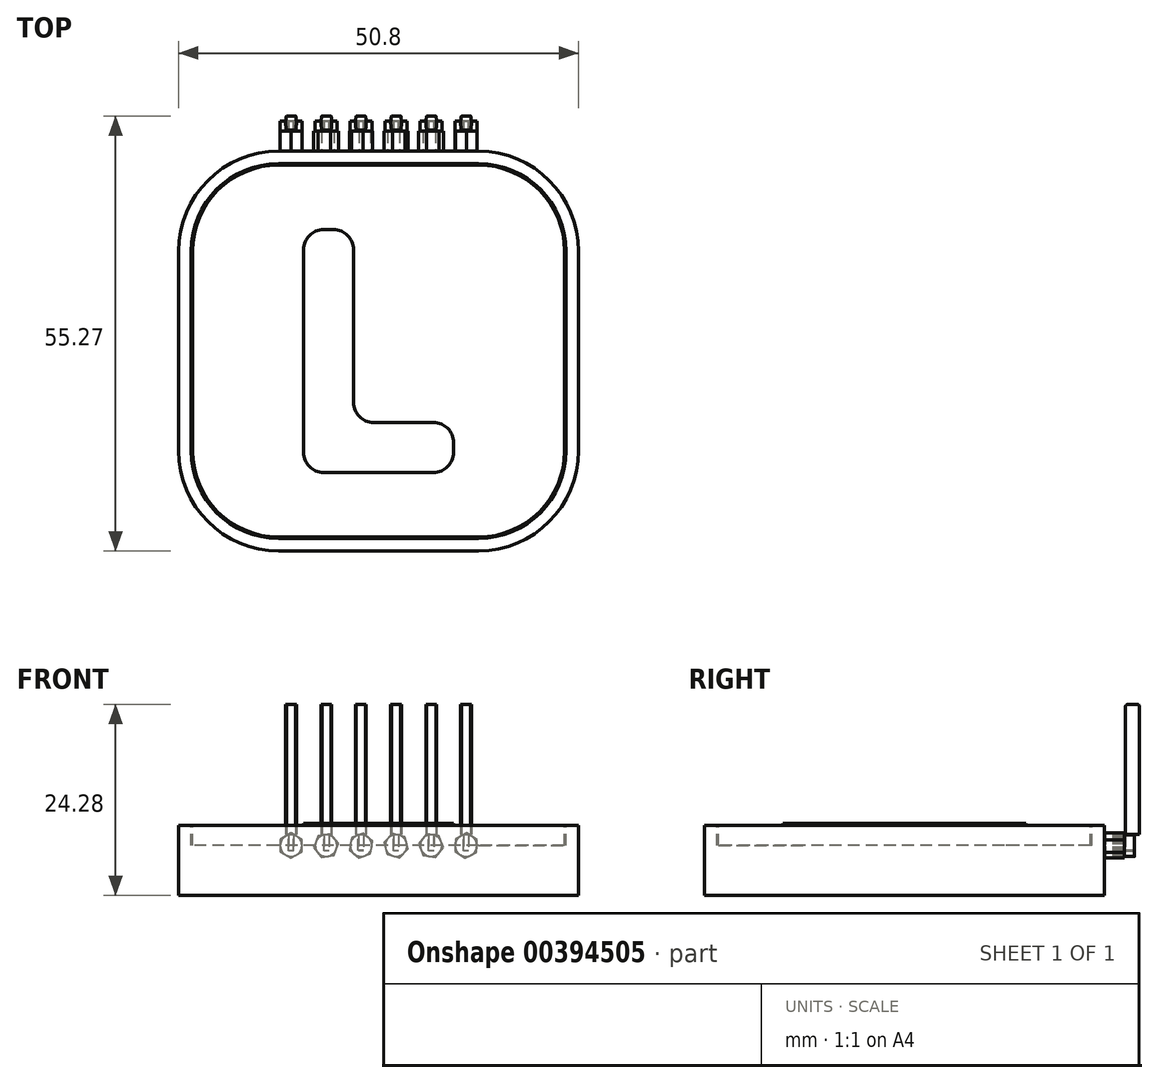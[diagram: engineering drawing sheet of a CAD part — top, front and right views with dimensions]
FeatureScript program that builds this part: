
annotation { "Feature Type Name" : "Feature", "Feature Type Description" : "" }
export const myFeature = defineFeature(function(context is Context, id is Id, definition is map)
    precondition{}
    {
        {
            var Q0;
            Q0=qCreatedBy(makeId("Top.planeOp"),FACE);
            var sketch = newSketch(context, id + "F0", { "sketchPlane" : qUnion([Q0])});
            skLineSegment(sketch, "E0.bottom", {"start": v(-25.4, 25.4) * mm, "end": v(25.4, 25.4) * mm});
            skLineSegment(sketch, "E0.top", {"start": v(-25.4, -25.4) * mm, "end": v(25.4, -25.4) * mm});
            skLineSegment(sketch, "E0.left", {"start": v(-25.4, 25.4) * mm, "end": v(-25.4, -25.4) * mm});
            skLineSegment(sketch, "E0.right", {"start": v(25.4, 25.4) * mm, "end": v(25.4, -25.4) * mm});
            skSolve(sketch);
        }
        {
            var Q0;
            Q0=makeQuery(id+"F0.imprint","IMPRINT",FACE,{"disambiguationData":[TD([[makeQuery(id+"F0.imprint","IMPRINT",EDGE,{"derivedFrom":sQuery(id+"F0.wireOp",EDGE,"E0.bottom")}),-1.0]])]});
            extrude(context, id + "F1", {"entities" : qUnion([Q0]), "depth" : 8.9 * mm});
        }
        {
            var Q0;
            Q0=makeQuery(id+"F1.opExtrude","SWEPT_EDGE",EDGE,{"disambiguationData":[OSD([sQuery(id+"F0.wireOp",EDGE,"E0.top"),sQuery(id+"F0.wireOp",EDGE,"E0.left")])]});
            var Q1;
            Q1=makeQuery(id+"F1.opExtrude","SWEPT_EDGE",EDGE,{"disambiguationData":[OSD([sQuery(id+"F0.wireOp",EDGE,"E0.bottom"),sQuery(id+"F0.wireOp",EDGE,"E0.left")])]});
            var Q2;
            Q2=makeQuery(id+"F1.opExtrude","SWEPT_EDGE",EDGE,{"disambiguationData":[OSD([sQuery(id+"F0.wireOp",EDGE,"E0.top"),sQuery(id+"F0.wireOp",EDGE,"E0.right")])]});
            var Q3;
            Q3=makeQuery(id+"F1.opExtrude","SWEPT_EDGE",EDGE,{"disambiguationData":[OSD([sQuery(id+"F0.wireOp",EDGE,"E0.bottom"),sQuery(id+"F0.wireOp",EDGE,"E0.right")])]});
            fillet(context, id + "F2", {"entities" : qUnion([Q0, Q1, Q2, Q3]), "radius" : 12.7 * mm, "tangentPropagation" : true, "allowEdgeOverflow" : false});
        }
        {
            var Q0;
            Q0=makeQuery(id+"F1.opExtrude","CAP_FACE",FACE,{"disambiguationData":[OSD([sQuery(id+"F0.wireOp",EDGE,"E0.bottom"),sQuery(id+"F0.wireOp",EDGE,"E0.top"),sQuery(id+"F0.wireOp",EDGE,"E0.left"),sQuery(id+"F0.wireOp",EDGE,"E0.right")])],"isStart":false});
            var sketch = newSketch(context, id + "F3", { "sketchPlane" : qUnion([Q0])});
            skArc(sketch, "E1.0", {"start": v(-12.7, 23.81) * mm, "mid": v(-20.56, 20.56) * mm, "end": v(-23.81, 12.7) * mm});
            skLineSegment(sketch, "E1.1", {"start": v(12.7, 23.81) * mm, "end": v(-12.7, 23.81) * mm});
            skLineSegment(sketch, "E1.2", {"start": v(-23.81, 12.7) * mm, "end": v(-23.81, -12.7) * mm});
            skArc(sketch, "E1.3", {"start": v(23.81, 12.7) * mm, "mid": v(20.56, 20.56) * mm, "end": v(12.7, 23.81) * mm});
            skArc(sketch, "E1.4", {"start": v(-23.81, -12.7) * mm, "mid": v(-20.56, -20.56) * mm, "end": v(-12.7, -23.81) * mm});
            skLineSegment(sketch, "E1.5", {"start": v(-12.7, -23.81) * mm, "end": v(12.7, -23.81) * mm});
            skArc(sketch, "E1.6", {"start": v(12.7, -23.81) * mm, "mid": v(20.56, -20.56) * mm, "end": v(23.81, -12.7) * mm});
            skLineSegment(sketch, "E1.7", {"start": v(23.81, -12.7) * mm, "end": v(23.81, 12.7) * mm});
            skArc(sketch, "E2.0", {"start": v(-12.7, 23.62) * mm, "mid": v(-20.42, 20.42) * mm, "end": v(-23.62, 12.7) * mm});
            skLineSegment(sketch, "E2.1", {"start": v(12.7, 23.62) * mm, "end": v(-12.7, 23.62) * mm});
            skLineSegment(sketch, "E2.2", {"start": v(-23.62, 12.7) * mm, "end": v(-23.62, -12.7) * mm});
            skArc(sketch, "E2.3", {"start": v(23.62, 12.7) * mm, "mid": v(20.42, 20.42) * mm, "end": v(12.7, 23.62) * mm});
            skArc(sketch, "E2.4", {"start": v(-23.62, -12.7) * mm, "mid": v(-20.42, -20.42) * mm, "end": v(-12.7, -23.62) * mm});
            skLineSegment(sketch, "E2.5", {"start": v(-12.7, -23.62) * mm, "end": v(12.7, -23.62) * mm});
            skArc(sketch, "E2.6", {"start": v(12.7, -23.62) * mm, "mid": v(20.42, -20.42) * mm, "end": v(23.62, -12.7) * mm});
            skLineSegment(sketch, "E2.7", {"start": v(23.62, -12.7) * mm, "end": v(23.62, 12.7) * mm});
            skSolve(sketch);
        }
        {
            var Q0;
            Q0=makeQuery(id+"F3.imprint","IMPRINT",FACE,{"disambiguationData":[TD([[makeQuery(id+"F3.imprint","IMPRINT",EDGE,{"derivedFrom":sQuery(id+"F3.wireOp",EDGE,"E1.0")}),1.0]])]});
            extrude(context, id + "F4", {"entities" : qUnion([Q0]), "operationType" : NewBodyOperationType.REMOVE, "oppositeDirection" : true, "depth" : 2.54 * mm});
        }
        {
            var Q0;
            Q0=makeQuery(id+"F4.boolean.opBoolean","SPLIT",FACE,{"disambiguationData":[TD([makeQuery(id+"F4.opExtrude","SWEPT_FACE",FACE,{"disambiguationData":[OSD([sQuery(id+"F3.wireOp",EDGE,"E2.0")])]})])],"derivedFrom":makeQuery(id+"F1.opExtrude","CAP_FACE",FACE,{"disambiguationData":[OSD([sQuery(id+"F0.wireOp",EDGE,"E0.bottom"),sQuery(id+"F0.wireOp",EDGE,"E0.top"),sQuery(id+"F0.wireOp",EDGE,"E0.left"),sQuery(id+"F0.wireOp",EDGE,"E0.right")])],"isStart":false})});
            var sketch = newSketch(context, id + "F5", { "sketchPlane" : qUnion([Q0])});
            skLineSegment(sketch, "E3", {"start": v(-9.53, 15.42) * mm, "end": v(-9.52, -15.42) * mm});
            skLineSegment(sketch, "E4", {"start": v(-9.52, -15.42) * mm, "end": v(9.53, -15.42) * mm});
            skLineSegment(sketch, "E5", {"start": v(9.53, -9.07) * mm, "end": v(-3.18, -9.07) * mm});
            skLineSegment(sketch, "E6", {"start": v(-3.18, -9.07) * mm, "end": v(-3.18, 15.42) * mm});
            skLineSegment(sketch, "E7", {"start": v(-3.18, 15.42) * mm, "end": v(-9.53, 15.42) * mm});
            skLineSegment(sketch, "E8", {"start": v(9.53, -9.07) * mm, "end": v(9.53, -15.42) * mm});
            skLineSegment(sketch, "E9.0", {"start": v(9.78, -8.81) * mm, "end": v(-2.92, -8.81) * mm});
            skLineSegment(sketch, "E9.1", {"start": v(-2.92, 15.67) * mm, "end": v(-9.78, 15.67) * mm});
            skLineSegment(sketch, "E9.2", {"start": v(-9.78, 15.67) * mm, "end": v(-9.78, -15.67) * mm});
            skLineSegment(sketch, "E9.3", {"start": v(-2.92, -8.81) * mm, "end": v(-2.92, 15.67) * mm});
            skLineSegment(sketch, "E9.4", {"start": v(-9.78, -15.67) * mm, "end": v(9.78, -15.67) * mm});
            skLineSegment(sketch, "E9.5", {"start": v(9.78, -8.81) * mm, "end": v(9.78, -15.67) * mm});
            skSolve(sketch);
        }
        {
            var Q0;
            Q0=makeQuery(id+"F5.imprint","IMPRINT",FACE,{"disambiguationData":[TD([[makeQuery(id+"F5.imprint","IMPRINT",EDGE,{"derivedFrom":sQuery(id+"F5.wireOp",EDGE,"E3")}),1.0]])]});
            extrude(context, id + "F6", {"entities" : qUnion([Q0]), "depth" : 0.25 * mm});
        }
        {
            var Q0;
            Q0=makeQuery(id+"F6.opExtrude","SWEPT_EDGE",EDGE,{"disambiguationData":[OSD([sQuery(id+"F5.wireOp",EDGE,"E3"),sQuery(id+"F5.wireOp",EDGE,"E4")])]});
            var Q1;
            Q1=makeQuery(id+"F6.opExtrude","SWEPT_EDGE",EDGE,{"disambiguationData":[OSD([sQuery(id+"F5.wireOp",EDGE,"E4"),sQuery(id+"F5.wireOp",EDGE,"E8")])]});
            var Q2;
            Q2=makeQuery(id+"F6.opExtrude","SWEPT_EDGE",EDGE,{"disambiguationData":[OSD([sQuery(id+"F5.wireOp",EDGE,"E5"),sQuery(id+"F5.wireOp",EDGE,"E8")])]});
            var Q3;
            Q3=makeQuery(id+"F6.opExtrude","SWEPT_EDGE",EDGE,{"disambiguationData":[OSD([sQuery(id+"F5.wireOp",EDGE,"E5"),sQuery(id+"F5.wireOp",EDGE,"E6")])]});
            var Q4;
            Q4=makeQuery(id+"F6.opExtrude","SWEPT_EDGE",EDGE,{"disambiguationData":[OSD([sQuery(id+"F5.wireOp",EDGE,"E6"),sQuery(id+"F5.wireOp",EDGE,"E7")])]});
            var Q5;
            Q5=makeQuery(id+"F6.opExtrude","SWEPT_EDGE",EDGE,{"disambiguationData":[OSD([sQuery(id+"F5.wireOp",EDGE,"E3"),sQuery(id+"F5.wireOp",EDGE,"E7")])]});
            fillet(context, id + "F7", {"entities" : qUnion([Q0, Q1, Q2, Q3, Q4, Q5]), "radius" : 2.54 * mm, "tangentPropagation" : true, "allowEdgeOverflow" : false});
        }
        {
            var Q0;
            Q0=makeQuery(id+"F1.opExtrude","SWEPT_FACE",FACE,{"disambiguationData":[OSD([sQuery(id+"F0.wireOp",EDGE,"E0.bottom")])]});
            var sketch = newSketch(context, id + "F8", { "sketchPlane" : qUnion([Q0])});
            skLineSegment(sketch, "E10.0", {"start": v(-9.71, 5.6) * mm, "end": v(-11.06, 4.76) * mm});
            skLineSegment(sketch, "E10.1", {"start": v(-11.06, 4.76) * mm, "end": v(-12.46, 5.5) * mm});
            skLineSegment(sketch, "E10.2", {"start": v(-12.46, 5.5) * mm, "end": v(-12.51, 7.1) * mm});
            skLineSegment(sketch, "E10.3", {"start": v(-12.51, 7.1) * mm, "end": v(-11.17, 7.94) * mm});
            skLineSegment(sketch, "E10.4", {"start": v(-11.17, 7.94) * mm, "end": v(-9.77, 7.2) * mm});
            skLineSegment(sketch, "E10.5", {"start": v(-9.77, 7.2) * mm, "end": v(-9.71, 5.6) * mm});
            skLineSegment(sketch, "E11.0", {"start": v(-7.25, 4.87) * mm, "end": v(-8.24, 6.12) * mm});
            skLineSegment(sketch, "E11.1", {"start": v(-8.24, 6.12) * mm, "end": v(-7.65, 7.6) * mm});
            skLineSegment(sketch, "E11.2", {"start": v(-7.65, 7.6) * mm, "end": v(-6.08, 7.83) * mm});
            skLineSegment(sketch, "E11.3", {"start": v(-6.08, 7.83) * mm, "end": v(-5.1, 6.58) * mm});
            skLineSegment(sketch, "E11.4", {"start": v(-5.1, 6.58) * mm, "end": v(-5.68, 5.1) * mm});
            skLineSegment(sketch, "E11.5", {"start": v(-5.68, 5.1) * mm, "end": v(-7.25, 4.87) * mm});
            skLineSegment(sketch, "E12.0", {"start": v(-2.64, 4.82) * mm, "end": v(-3.76, 5.95) * mm});
            skLineSegment(sketch, "E12.1", {"start": v(-3.76, 5.95) * mm, "end": v(-3.34, 7.48) * mm});
            skLineSegment(sketch, "E12.2", {"start": v(-3.34, 7.48) * mm, "end": v(-1.8, 7.88) * mm});
            skLineSegment(sketch, "E12.3", {"start": v(-1.8, 7.88) * mm, "end": v(-0.69, 6.75) * mm});
            skLineSegment(sketch, "E12.4", {"start": v(-0.69, 6.75) * mm, "end": v(-1.1, 5.22) * mm});
            skLineSegment(sketch, "E12.5", {"start": v(-1.1, 5.22) * mm, "end": v(-2.64, 4.82) * mm});
            skLineSegment(sketch, "E13.0", {"start": v(2.47, 4.78) * mm, "end": v(0.99, 5.35) * mm});
            skLineSegment(sketch, "E13.1", {"start": v(0.99, 5.35) * mm, "end": v(0.74, 6.92) * mm});
            skLineSegment(sketch, "E13.2", {"start": v(0.74, 6.92) * mm, "end": v(1.97, 7.92) * mm});
            skLineSegment(sketch, "E13.3", {"start": v(1.97, 7.92) * mm, "end": v(3.46, 7.35) * mm});
            skLineSegment(sketch, "E13.4", {"start": v(3.46, 7.35) * mm, "end": v(3.7, 5.78) * mm});
            skLineSegment(sketch, "E13.5", {"start": v(3.7, 5.78) * mm, "end": v(2.47, 4.78) * mm});
            skLineSegment(sketch, "E14.0", {"start": v(5.67, 5.12) * mm, "end": v(5.1, 6.6) * mm});
            skLineSegment(sketch, "E14.1", {"start": v(5.1, 6.6) * mm, "end": v(6.1, 7.83) * mm});
            skLineSegment(sketch, "E14.2", {"start": v(6.1, 7.83) * mm, "end": v(7.67, 7.58) * mm});
            skLineSegment(sketch, "E14.3", {"start": v(7.67, 7.58) * mm, "end": v(8.23, 6.1) * mm});
            skLineSegment(sketch, "E14.4", {"start": v(8.23, 6.1) * mm, "end": v(7.23, 4.87) * mm});
            skLineSegment(sketch, "E14.5", {"start": v(7.23, 4.87) * mm, "end": v(5.67, 5.12) * mm});
            skLineSegment(sketch, "E15.0", {"start": v(11.11, 4.76) * mm, "end": v(9.74, 5.56) * mm});
            skLineSegment(sketch, "E15.1", {"start": v(9.74, 5.56) * mm, "end": v(9.74, 7.14) * mm});
            skLineSegment(sketch, "E15.2", {"start": v(9.74, 7.14) * mm, "end": v(11.11, 7.94) * mm});
            skLineSegment(sketch, "E15.3", {"start": v(11.11, 7.94) * mm, "end": v(12.49, 7.14) * mm});
            skLineSegment(sketch, "E15.4", {"start": v(12.49, 7.14) * mm, "end": v(12.49, 5.56) * mm});
            skLineSegment(sketch, "E15.5", {"start": v(12.49, 5.56) * mm, "end": v(11.11, 4.76) * mm});
            skSolve(sketch);
        }
        {
            var Q0;
            Q0=makeQuery(id+"F8.imprint","IMPRINT",FACE,{"disambiguationData":[TD([[makeQuery(id+"F8.imprint","IMPRINT",EDGE,{"derivedFrom":sQuery(id+"F8.wireOp",EDGE,"E10.0")}),-1.0]])]});
            var Q1;
            Q1=makeQuery(id+"F8.imprint","IMPRINT",FACE,{"disambiguationData":[TD([[makeQuery(id+"F8.imprint","IMPRINT",EDGE,{"derivedFrom":sQuery(id+"F8.wireOp",EDGE,"E11.0")}),-1.0]])]});
            var Q2;
            Q2=makeQuery(id+"F8.imprint","IMPRINT",FACE,{"disambiguationData":[TD([[makeQuery(id+"F8.imprint","IMPRINT",EDGE,{"derivedFrom":sQuery(id+"F8.wireOp",EDGE,"E12.0")}),-1.0]])]});
            var Q3;
            Q3=makeQuery(id+"F8.imprint","IMPRINT",FACE,{"disambiguationData":[TD([[makeQuery(id+"F8.imprint","IMPRINT",EDGE,{"derivedFrom":sQuery(id+"F8.wireOp",EDGE,"E13.0")}),-1.0]])]});
            var Q4;
            Q4=makeQuery(id+"F8.imprint","IMPRINT",FACE,{"disambiguationData":[TD([[makeQuery(id+"F8.imprint","IMPRINT",EDGE,{"derivedFrom":sQuery(id+"F8.wireOp",EDGE,"E14.0")}),-1.0]])]});
            var Q5;
            Q5=makeQuery(id+"F8.imprint","IMPRINT",FACE,{"disambiguationData":[TD([[makeQuery(id+"F8.imprint","IMPRINT",EDGE,{"derivedFrom":sQuery(id+"F8.wireOp",EDGE,"E15.0")}),-1.0]])]});
            extrude(context, id + "F9", {"entities" : qUnion([Q0, Q1, Q2, Q3, Q4, Q5]), "operationType" : NewBodyOperationType.ADD, "depth" : 2.54 * mm});
        }
        {
            var Q0;
            Q0=makeQuery(id+"F9.opExtrude","CAP_FACE",FACE,{"disambiguationData":[OSD([sQuery(id+"F8.wireOp",EDGE,"E10.0"),sQuery(id+"F8.wireOp",EDGE,"E10.1"),sQuery(id+"F8.wireOp",EDGE,"E10.2"),sQuery(id+"F8.wireOp",EDGE,"E10.3"),sQuery(id+"F8.wireOp",EDGE,"E10.4"),sQuery(id+"F8.wireOp",EDGE,"E10.5")])],"isStart":false});
            var sketch = newSketch(context, id + "F10", { "sketchPlane" : qUnion([Q0])});
            skCircle(sketch, "E16", {"center": v(-11.11, 6.35) * mm, "radius": 1.37 * mm});
            skSolve(sketch);
        }
        {
            var Q0;
            Q0=makeQuery(id+"F9.opExtrude","CAP_FACE",FACE,{"disambiguationData":[OSD([sQuery(id+"F8.wireOp",EDGE,"E11.0"),sQuery(id+"F8.wireOp",EDGE,"E11.1"),sQuery(id+"F8.wireOp",EDGE,"E11.2"),sQuery(id+"F8.wireOp",EDGE,"E11.3"),sQuery(id+"F8.wireOp",EDGE,"E11.4"),sQuery(id+"F8.wireOp",EDGE,"E11.5")])],"isStart":false});
            var sketch = newSketch(context, id + "F11", { "sketchPlane" : qUnion([Q0])});
            skCircle(sketch, "E17", {"center": v(-6.67, 6.35) * mm, "radius": 1.37 * mm});
            skSolve(sketch);
        }
        {
            var Q0;
            Q0=makeQuery(id+"F9.opExtrude","CAP_FACE",FACE,{"disambiguationData":[OSD([sQuery(id+"F8.wireOp",EDGE,"E12.0"),sQuery(id+"F8.wireOp",EDGE,"E12.1"),sQuery(id+"F8.wireOp",EDGE,"E12.2"),sQuery(id+"F8.wireOp",EDGE,"E12.3"),sQuery(id+"F8.wireOp",EDGE,"E12.4"),sQuery(id+"F8.wireOp",EDGE,"E12.5")])],"isStart":false});
            var sketch = newSketch(context, id + "F12", { "sketchPlane" : qUnion([Q0])});
            skCircle(sketch, "E18", {"center": v(-2.22, 6.35) * mm, "radius": 1.37 * mm});
            skSolve(sketch);
        }
        {
            var Q0;
            Q0=makeQuery(id+"F9.opExtrude","CAP_FACE",FACE,{"disambiguationData":[OSD([sQuery(id+"F8.wireOp",EDGE,"E13.0"),sQuery(id+"F8.wireOp",EDGE,"E13.1"),sQuery(id+"F8.wireOp",EDGE,"E13.2"),sQuery(id+"F8.wireOp",EDGE,"E13.3"),sQuery(id+"F8.wireOp",EDGE,"E13.4"),sQuery(id+"F8.wireOp",EDGE,"E13.5")])],"isStart":false});
            var sketch = newSketch(context, id + "F13", { "sketchPlane" : qUnion([Q0])});
            skCircle(sketch, "E19", {"center": v(2.22, 6.35) * mm, "radius": 1.37 * mm});
            skSolve(sketch);
        }
        {
            var Q0;
            Q0=makeQuery(id+"F9.opExtrude","CAP_FACE",FACE,{"disambiguationData":[OSD([sQuery(id+"F8.wireOp",EDGE,"E14.0"),sQuery(id+"F8.wireOp",EDGE,"E14.1"),sQuery(id+"F8.wireOp",EDGE,"E14.2"),sQuery(id+"F8.wireOp",EDGE,"E14.3"),sQuery(id+"F8.wireOp",EDGE,"E14.4"),sQuery(id+"F8.wireOp",EDGE,"E14.5")])],"isStart":false});
            var sketch = newSketch(context, id + "F14", { "sketchPlane" : qUnion([Q0])});
            skCircle(sketch, "E20", {"center": v(6.67, 6.35) * mm, "radius": 1.37 * mm});
            skSolve(sketch);
        }
        {
            var Q0;
            Q0=makeQuery(id+"F9.opExtrude","CAP_FACE",FACE,{"disambiguationData":[OSD([sQuery(id+"F8.wireOp",EDGE,"E15.0"),sQuery(id+"F8.wireOp",EDGE,"E15.1"),sQuery(id+"F8.wireOp",EDGE,"E15.2"),sQuery(id+"F8.wireOp",EDGE,"E15.3"),sQuery(id+"F8.wireOp",EDGE,"E15.4"),sQuery(id+"F8.wireOp",EDGE,"E15.5")])],"isStart":false});
            var sketch = newSketch(context, id + "F15", { "sketchPlane" : qUnion([Q0])});
            skCircle(sketch, "E21", {"center": v(11.11, 6.35) * mm, "radius": 1.37 * mm});
            skSolve(sketch);
        }
        {
            var Q0;
            {var subQ0=sQuery(id+"F10.wireOp",EDGE,"E16");var subQ4=makeQuery(id+"F10.imprint","INTERSECT",VERTEX,{"derivedFrom":[makeQuery(id+"F9.opExtrude","CAP_EDGE",EDGE,{"disambiguationData":[OSD([sQuery(id+"F8.wireOp",EDGE,"E10.4")])],"isStart":false}),subQ0]});Q0=makeQuery(id+"F10.imprint","IMPRINT",FACE,{"disambiguationData":[TD([[makeQuery(id+"F10.imprint","IMPRINT",EDGE,{"disambiguationData":[TD([[subQ4,1.0]])],"derivedFrom":subQ0}),1.0]])]});}
            var Q1;
            {var subQ0=sQuery(id+"F11.wireOp",EDGE,"E17");var subQ4=makeQuery(id+"F11.imprint","INTERSECT",VERTEX,{"derivedFrom":[makeQuery(id+"F9.opExtrude","CAP_EDGE",EDGE,{"disambiguationData":[OSD([sQuery(id+"F8.wireOp",EDGE,"E11.2")])],"isStart":false}),subQ0]});Q1=makeQuery(id+"F11.imprint","IMPRINT",FACE,{"disambiguationData":[TD([[makeQuery(id+"F11.imprint","IMPRINT",EDGE,{"disambiguationData":[TD([[subQ4,1.0]])],"derivedFrom":subQ0}),1.0]])]});}
            var Q2;
            {var subQ0=sQuery(id+"F12.wireOp",EDGE,"E18");var subQ4=makeQuery(id+"F12.imprint","INTERSECT",VERTEX,{"derivedFrom":[makeQuery(id+"F9.opExtrude","CAP_EDGE",EDGE,{"disambiguationData":[OSD([sQuery(id+"F8.wireOp",EDGE,"E12.2")])],"isStart":false}),subQ0]});Q2=makeQuery(id+"F12.imprint","IMPRINT",FACE,{"disambiguationData":[TD([[makeQuery(id+"F12.imprint","IMPRINT",EDGE,{"disambiguationData":[TD([[subQ4,1.0]])],"derivedFrom":subQ0}),1.0]])]});}
            var Q3;
            {var subQ0=sQuery(id+"F13.wireOp",EDGE,"E19");var subQ4=makeQuery(id+"F13.imprint","INTERSECT",VERTEX,{"derivedFrom":[makeQuery(id+"F9.opExtrude","CAP_EDGE",EDGE,{"disambiguationData":[OSD([sQuery(id+"F8.wireOp",EDGE,"E13.3")])],"isStart":false}),subQ0]});Q3=makeQuery(id+"F13.imprint","IMPRINT",FACE,{"disambiguationData":[TD([[makeQuery(id+"F13.imprint","IMPRINT",EDGE,{"disambiguationData":[TD([[subQ4,1.0]])],"derivedFrom":subQ0}),1.0]])]});}
            var Q4;
            {var subQ0=sQuery(id+"F14.wireOp",EDGE,"E20");var subQ4=makeQuery(id+"F14.imprint","INTERSECT",VERTEX,{"derivedFrom":[makeQuery(id+"F9.opExtrude","CAP_EDGE",EDGE,{"disambiguationData":[OSD([sQuery(id+"F8.wireOp",EDGE,"E14.2")])],"isStart":false}),subQ0]});Q4=makeQuery(id+"F14.imprint","IMPRINT",FACE,{"disambiguationData":[TD([[makeQuery(id+"F14.imprint","IMPRINT",EDGE,{"disambiguationData":[TD([[subQ4,1.0]])],"derivedFrom":subQ0}),1.0]])]});}
            var Q5;
            {var subQ0=sQuery(id+"F15.wireOp",EDGE,"E21");var subQ4=makeQuery(id+"F15.imprint","INTERSECT",VERTEX,{"derivedFrom":[makeQuery(id+"F9.opExtrude","CAP_EDGE",EDGE,{"disambiguationData":[OSD([sQuery(id+"F8.wireOp",EDGE,"E15.3")])],"isStart":false}),subQ0]});Q5=makeQuery(id+"F15.imprint","IMPRINT",FACE,{"disambiguationData":[TD([[makeQuery(id+"F15.imprint","IMPRINT",EDGE,{"disambiguationData":[TD([[subQ4,1.0]])],"derivedFrom":subQ0}),1.0]])]});}
            extrude(context, id + "F16", {"entities" : qUnion([Q0, Q1, Q2, Q3, Q4, Q5]), "operationType" : NewBodyOperationType.ADD, "depth" : 1.27 * mm});
        }
        {
            var Q0;
            Q0=makeQuery(id+"F16.opExtrude","CAP_FACE",FACE,{"disambiguationData":[OSD([sQuery(id+"F10.wireOp",EDGE,"E16")])],"isStart":false});
            var sketch = newSketch(context, id + "F17", { "sketchPlane" : qUnion([Q0])});
            skLineSegment(sketch, "E22", {"start": v(-11.44, 7.69) * mm, "end": v(-11.44, 5.67) * mm});
            skLineSegment(sketch, "E23", {"start": v(-11.44, 5.67) * mm, "end": v(-10.77, 5.67) * mm});
            skLineSegment(sketch, "E24", {"start": v(-10.77, 5.67) * mm, "end": v(-10.77, 7.68) * mm});
            skLineSegment(sketch, "E25", {"start": v(-11.44, 7.69) * mm, "end": v(-11.44, 7.98) * mm});
            skLineSegment(sketch, "E26", {"start": v(-11.44, 7.98) * mm, "end": v(-10.77, 7.98) * mm});
            skLineSegment(sketch, "E27", {"start": v(-10.77, 7.68) * mm, "end": v(-10.77, 7.98) * mm});
            skSolve(sketch);
        }
        {
            var Q0;
            Q0=makeQuery(id+"F16.opExtrude","CAP_FACE",FACE,{"disambiguationData":[OSD([sQuery(id+"F11.wireOp",EDGE,"E17")])],"isStart":false});
            var sketch = newSketch(context, id + "F18", { "sketchPlane" : qUnion([Q0])});
            skLineSegment(sketch, "E28", {"start": v(-7.01, 7.68) * mm, "end": v(-7.01, 5.67) * mm});
            skLineSegment(sketch, "E29", {"start": v(-7.01, 5.67) * mm, "end": v(-6.34, 5.67) * mm});
            skLineSegment(sketch, "E30", {"start": v(-6.34, 5.67) * mm, "end": v(-6.34, 7.68) * mm});
            skLineSegment(sketch, "E31", {"start": v(-7.01, 7.68) * mm, "end": v(-7.01, 7.98) * mm});
            skLineSegment(sketch, "E32", {"start": v(-7.01, 7.98) * mm, "end": v(-6.34, 7.98) * mm});
            skLineSegment(sketch, "E33", {"start": v(-6.34, 7.68) * mm, "end": v(-6.34, 7.98) * mm});
            skSolve(sketch);
        }
        {
            var Q0;
            Q0=makeQuery(id+"F16.opExtrude","CAP_FACE",FACE,{"disambiguationData":[OSD([sQuery(id+"F12.wireOp",EDGE,"E18")])],"isStart":false});
            var sketch = newSketch(context, id + "F19", { "sketchPlane" : qUnion([Q0])});
            skLineSegment(sketch, "E34", {"start": v(-2.57, 7.7) * mm, "end": v(-2.57, 5.7) * mm});
            skLineSegment(sketch, "E35", {"start": v(-2.57, 5.7) * mm, "end": v(-1.9, 5.7) * mm});
            skLineSegment(sketch, "E36", {"start": v(-1.9, 5.7) * mm, "end": v(-1.9, 7.7) * mm});
            skLineSegment(sketch, "E37", {"start": v(-2.57, 7.7) * mm, "end": v(-2.57, 8) * mm});
            skLineSegment(sketch, "E38", {"start": v(-2.57, 8) * mm, "end": v(-1.9, 8) * mm});
            skLineSegment(sketch, "E39", {"start": v(-1.9, 7.7) * mm, "end": v(-1.9, 8) * mm});
            skSolve(sketch);
        }
        {
            var Q0;
            Q0=makeQuery(id+"F16.opExtrude","CAP_FACE",FACE,{"disambiguationData":[OSD([sQuery(id+"F13.wireOp",EDGE,"E19")])],"isStart":false});
            var sketch = newSketch(context, id + "F20", { "sketchPlane" : qUnion([Q0])});
            skLineSegment(sketch, "E40", {"start": v(1.92, 7.73) * mm, "end": v(1.92, 5.72) * mm});
            skLineSegment(sketch, "E41", {"start": v(1.92, 5.72) * mm, "end": v(2.59, 5.72) * mm});
            skLineSegment(sketch, "E42", {"start": v(2.59, 5.72) * mm, "end": v(2.59, 7.73) * mm});
            skLineSegment(sketch, "E43", {"start": v(1.92, 7.73) * mm, "end": v(1.92, 8.03) * mm});
            skLineSegment(sketch, "E44", {"start": v(1.92, 8.03) * mm, "end": v(2.59, 8.03) * mm});
            skLineSegment(sketch, "E45", {"start": v(2.59, 7.73) * mm, "end": v(2.59, 8.03) * mm});
            skSolve(sketch);
        }
        {
            var Q0;
            Q0=makeQuery(id+"F16.opExtrude","CAP_FACE",FACE,{"disambiguationData":[OSD([sQuery(id+"F14.wireOp",EDGE,"E20")])],"isStart":false});
            var sketch = newSketch(context, id + "F21", { "sketchPlane" : qUnion([Q0])});
            skLineSegment(sketch, "E46", {"start": v(6.28, 7.72) * mm, "end": v(6.28, 5.7) * mm});
            skLineSegment(sketch, "E47", {"start": v(6.28, 5.7) * mm, "end": v(6.95, 5.7) * mm});
            skLineSegment(sketch, "E48", {"start": v(6.95, 5.7) * mm, "end": v(6.95, 7.72) * mm});
            skLineSegment(sketch, "E49", {"start": v(6.28, 7.72) * mm, "end": v(6.28, 8.02) * mm});
            skLineSegment(sketch, "E50", {"start": v(6.28, 8.02) * mm, "end": v(6.95, 8.02) * mm});
            skLineSegment(sketch, "E51", {"start": v(6.95, 7.72) * mm, "end": v(6.95, 8.02) * mm});
            skLineSegment(sketch, "E52", {"start": v(10.78, 7.72) * mm, "end": v(10.78, 5.7) * mm});
            skLineSegment(sketch, "E53", {"start": v(10.78, 5.7) * mm, "end": v(11.46, 5.7) * mm});
            skLineSegment(sketch, "E54", {"start": v(11.46, 5.7) * mm, "end": v(11.46, 7.72) * mm});
            skLineSegment(sketch, "E55", {"start": v(10.78, 7.72) * mm, "end": v(10.78, 8.02) * mm});
            skLineSegment(sketch, "E56", {"start": v(10.78, 8.02) * mm, "end": v(11.46, 8.02) * mm});
            skLineSegment(sketch, "E57", {"start": v(11.46, 7.72) * mm, "end": v(11.46, 8.02) * mm});
            skSolve(sketch);
        }
        {
            var Q0;
            {var subQ0=sQuery(id+"F17.wireOp",EDGE,"E22");Q0=makeQuery(id+"F17.imprint","IMPRINT",FACE,{"disambiguationData":[TD([[makeQuery(id+"F17.imprint","IMPRINT",EDGE,{"derivedFrom":subQ0}),1.0]])]});}
            var Q1;
            {var subQ1=sQuery(id+"F18.wireOp",EDGE,"E29");Q1=makeQuery(id+"F18.imprint","IMPRINT",FACE,{"disambiguationData":[TD([[makeQuery(id+"F18.imprint","IMPRINT",EDGE,{"derivedFrom":subQ1}),1.0]])]});}
            var Q2;
            {var subQ0=sQuery(id+"F19.wireOp",EDGE,"E35");Q2=makeQuery(id+"F19.imprint","IMPRINT",FACE,{"disambiguationData":[TD([[makeQuery(id+"F19.imprint","IMPRINT",EDGE,{"derivedFrom":subQ0}),1.0]])]});}
            var Q3;
            {var subQ0=sQuery(id+"F20.wireOp",EDGE,"E41");Q3=makeQuery(id+"F20.imprint","IMPRINT",FACE,{"disambiguationData":[TD([[makeQuery(id+"F20.imprint","IMPRINT",EDGE,{"derivedFrom":subQ0}),1.0]])]});}
            var Q4;
            {var subQ0=sQuery(id+"F21.wireOp",EDGE,"E47");Q4=makeQuery(id+"F21.imprint","IMPRINT",FACE,{"disambiguationData":[TD([[makeQuery(id+"F21.imprint","IMPRINT",EDGE,{"derivedFrom":subQ0}),1.0]])]});}
            var Q5;
            Q5=makeQuery(id+"F21.imprint","IMPRINT",FACE,{"disambiguationData":[TD([[makeQuery(id+"F21.imprint","IMPRINT",EDGE,{"derivedFrom":sQuery(id+"F21.wireOp",EDGE,"E52")}),1.0]])]});
            extrude(context, id + "F22", {"entities" : qUnion([Q0, Q1, Q2, Q3, Q4, Q5]), "operationType" : NewBodyOperationType.REMOVE, "oppositeDirection" : true, "depth" : 1.14 * mm});
        }
        {
            var Q0;
            Q0=makeQuery(id+"F22.boolean.opBoolean","COPY",FACE,{"derivedFrom":makeQuery(id+"F22.opExtrude","SWEPT_FACE",FACE,{"disambiguationData":[OSD([sQuery(id+"F17.wireOp",EDGE,"E23")])]})});
            cPlane(context, id + "F23", {"entities" : qUnion([Q0]), "cplaneType" : CPlaneType.OFFSET, "offset" : 0.06 * mm, "width" : 152.4 * mm, "height" : 152.4 * mm});
        }
        {
            var Q0;
            Q0=qCreatedBy(id+"F23.planeOp",FACE);
            var sketch = newSketch(context, id + "F24", { "sketchPlane" : qUnion([Q0])});
            skLineSegment(sketch, "E58.bottom", {"start": v(10.78, 29.2) * mm, "end": v(11.42, 29.2) * mm});
            skLineSegment(sketch, "E58.top", {"start": v(10.78, 28.08) * mm, "end": v(11.42, 28.08) * mm});
            skLineSegment(sketch, "E58.left", {"start": v(10.78, 29.2) * mm, "end": v(10.78, 28.08) * mm});
            skLineSegment(sketch, "E58.right", {"start": v(11.42, 29.2) * mm, "end": v(11.42, 28.08) * mm});
            skLineSegment(sketch, "E59.bottom", {"start": v(6.36, 29.2) * mm, "end": v(7, 29.2) * mm});
            skLineSegment(sketch, "E59.top", {"start": v(6.36, 28.08) * mm, "end": v(7, 28.08) * mm});
            skLineSegment(sketch, "E59.left", {"start": v(6.36, 29.2) * mm, "end": v(6.36, 28.08) * mm});
            skLineSegment(sketch, "E59.right", {"start": v(7, 29.2) * mm, "end": v(7, 28.08) * mm});
            skLineSegment(sketch, "E60.bottom", {"start": v(1.9, 29.2) * mm, "end": v(2.55, 29.2) * mm});
            skLineSegment(sketch, "E60.top", {"start": v(1.9, 28.08) * mm, "end": v(2.55, 28.08) * mm});
            skLineSegment(sketch, "E60.left", {"start": v(1.9, 29.2) * mm, "end": v(1.9, 28.08) * mm});
            skLineSegment(sketch, "E60.right", {"start": v(2.55, 29.2) * mm, "end": v(2.55, 28.08) * mm});
            skLineSegment(sketch, "E61.bottom", {"start": v(-2.58, 29.2) * mm, "end": v(-1.94, 29.2) * mm});
            skLineSegment(sketch, "E61.top", {"start": v(-2.58, 28.08) * mm, "end": v(-1.94, 28.08) * mm});
            skLineSegment(sketch, "E61.left", {"start": v(-2.58, 29.2) * mm, "end": v(-2.58, 28.08) * mm});
            skLineSegment(sketch, "E61.right", {"start": v(-1.94, 29.2) * mm, "end": v(-1.94, 28.08) * mm});
            skLineSegment(sketch, "E62.bottom", {"start": v(-6.93, 29.2) * mm, "end": v(-6.3, 29.2) * mm});
            skLineSegment(sketch, "E62.top", {"start": v(-6.93, 28.08) * mm, "end": v(-6.3, 28.08) * mm});
            skLineSegment(sketch, "E62.left", {"start": v(-6.93, 29.2) * mm, "end": v(-6.93, 28.08) * mm});
            skLineSegment(sketch, "E62.right", {"start": v(-6.3, 29.2) * mm, "end": v(-6.3, 28.08) * mm});
            skLineSegment(sketch, "E63.bottom", {"start": v(-11.44, 29.2) * mm, "end": v(-10.8, 29.2) * mm});
            skLineSegment(sketch, "E63.top", {"start": v(-11.44, 28.08) * mm, "end": v(-10.8, 28.08) * mm});
            skLineSegment(sketch, "E63.left", {"start": v(-11.44, 29.2) * mm, "end": v(-11.44, 28.08) * mm});
            skLineSegment(sketch, "E63.right", {"start": v(-10.8, 29.2) * mm, "end": v(-10.8, 28.08) * mm});
            skSolve(sketch);
        }
        {
            var Q0;
            Q0 = qSketchRegion(id + "F24", true);
            extrude(context, id + "F25", {"entities" : qUnion([Q0]), "depth" : 2.03 * mm});
        }
        {
            var Q0;
            Q0=makeQuery(id+"F25.opExtrude","CAP_FACE",FACE,{"disambiguationData":[OSD([sQuery(id+"F24.wireOp",EDGE,"E58.bottom"),sQuery(id+"F24.wireOp",EDGE,"E58.top"),sQuery(id+"F24.wireOp",EDGE,"E58.left"),sQuery(id+"F24.wireOp",EDGE,"E58.right")])],"isStart":false});
            cPlane(context, id + "F26", {"entities" : qUnion([Q0]), "cplaneType" : CPlaneType.OFFSET, "offset" : 0 * mm, "width" : 152.4 * mm, "height" : 152.4 * mm});
        }
        {
            var Q0;
            Q0=qCreatedBy(id+"F26.planeOp",FACE);
            var sketch = newSketch(context, id + "F27", { "sketchPlane" : qUnion([Q0])});
            skLineSegment(sketch, "E64", {"start": v(10.53, 28.09) * mm, "end": v(11.7, 28.09) * mm});
            skArc(sketch, "E65", {"start": v(10.53, 29.87) * mm, "mid": v(10.43, 28.98) * mm, "end": v(10.53, 28.09) * mm});
            skArc(sketch, "E66", {"start": v(11.7, 28.09) * mm, "mid": v(11.8, 28.98) * mm, "end": v(11.7, 29.87) * mm});
            skLineSegment(sketch, "E67", {"start": v(10.53, 29.87) * mm, "end": v(11.7, 29.87) * mm});
            skLineSegment(sketch, "E68", {"start": v(6.11, 28.09) * mm, "end": v(7.28, 28.09) * mm});
            skArc(sketch, "E69", {"start": v(6.11, 29.87) * mm, "mid": v(6.02, 28.98) * mm, "end": v(6.11, 28.09) * mm});
            skArc(sketch, "E70", {"start": v(7.28, 28.09) * mm, "mid": v(7.38, 28.98) * mm, "end": v(7.28, 29.87) * mm});
            skLineSegment(sketch, "E71", {"start": v(6.11, 29.87) * mm, "end": v(7.28, 29.87) * mm});
            skLineSegment(sketch, "E72", {"start": v(1.64, 28.09) * mm, "end": v(2.81, 28.09) * mm});
            skArc(sketch, "E73", {"start": v(1.64, 29.87) * mm, "mid": v(1.55, 28.98) * mm, "end": v(1.64, 28.09) * mm});
            skArc(sketch, "E74", {"start": v(2.81, 28.09) * mm, "mid": v(2.91, 28.98) * mm, "end": v(2.81, 29.87) * mm});
            skLineSegment(sketch, "E75", {"start": v(1.64, 29.87) * mm, "end": v(2.81, 29.87) * mm});
            skLineSegment(sketch, "E76", {"start": v(-2.84, 28.09) * mm, "end": v(-1.67, 28.09) * mm});
            skArc(sketch, "E77", {"start": v(-2.84, 29.87) * mm, "mid": v(-2.93, 28.98) * mm, "end": v(-2.84, 28.09) * mm});
            skArc(sketch, "E78", {"start": v(-1.67, 28.09) * mm, "mid": v(-1.57, 28.98) * mm, "end": v(-1.67, 29.87) * mm});
            skLineSegment(sketch, "E79", {"start": v(-2.84, 29.87) * mm, "end": v(-1.67, 29.87) * mm});
            skLineSegment(sketch, "E80", {"start": v(-7.21, 28.09) * mm, "end": v(-6.04, 28.09) * mm});
            skArc(sketch, "E81", {"start": v(-7.21, 29.87) * mm, "mid": v(-7.3, 28.98) * mm, "end": v(-7.21, 28.09) * mm});
            skArc(sketch, "E82", {"start": v(-6.04, 28.09) * mm, "mid": v(-5.94, 28.98) * mm, "end": v(-6.04, 29.87) * mm});
            skLineSegment(sketch, "E83", {"start": v(-7.21, 29.87) * mm, "end": v(-6.04, 29.87) * mm});
            skLineSegment(sketch, "E84", {"start": v(-11.7, 28.09) * mm, "end": v(-10.53, 28.09) * mm});
            skArc(sketch, "E85", {"start": v(-11.7, 29.87) * mm, "mid": v(-11.8, 28.98) * mm, "end": v(-11.7, 28.09) * mm});
            skArc(sketch, "E86", {"start": v(-10.53, 28.09) * mm, "mid": v(-10.44, 28.98) * mm, "end": v(-10.53, 29.87) * mm});
            skLineSegment(sketch, "E87", {"start": v(-11.7, 29.87) * mm, "end": v(-10.53, 29.87) * mm});
            skSolve(sketch);
        }
        {
            var Q0;
            Q0 = qSketchRegion(id + "F27", true);
            extrude(context, id + "F28", {"entities" : qUnion([Q0]), "depth" : 16.5 * mm});
        }
        {
            var Q0;
            Q0=makeQuery(id+"F28.opExtrude","CAP_EDGE",EDGE,{"disambiguationData":[OSD([sQuery(id+"F27.wireOp",EDGE,"E84")])],"isStart":false});
            var Q1;
            Q1=makeQuery(id+"F28.opExtrude","CAP_EDGE",EDGE,{"disambiguationData":[OSD([sQuery(id+"F27.wireOp",EDGE,"E87")])],"isStart":false});
            var Q2;
            Q2=makeQuery(id+"F28.opExtrude","CAP_EDGE",EDGE,{"disambiguationData":[OSD([sQuery(id+"F27.wireOp",EDGE,"E83")])],"isStart":false});
            var Q3;
            Q3=makeQuery(id+"F28.opExtrude","CAP_EDGE",EDGE,{"disambiguationData":[OSD([sQuery(id+"F27.wireOp",EDGE,"E80")])],"isStart":false});
            var Q4;
            Q4=makeQuery(id+"F28.opExtrude","CAP_EDGE",EDGE,{"disambiguationData":[OSD([sQuery(id+"F27.wireOp",EDGE,"E76")])],"isStart":false});
            var Q5;
            Q5=makeQuery(id+"F28.opExtrude","CAP_EDGE",EDGE,{"disambiguationData":[OSD([sQuery(id+"F27.wireOp",EDGE,"E79")])],"isStart":false});
            var Q6;
            Q6=makeQuery(id+"F28.opExtrude","CAP_EDGE",EDGE,{"disambiguationData":[OSD([sQuery(id+"F27.wireOp",EDGE,"E72")])],"isStart":false});
            var Q7;
            Q7=makeQuery(id+"F28.opExtrude","CAP_EDGE",EDGE,{"disambiguationData":[OSD([sQuery(id+"F27.wireOp",EDGE,"E75")])],"isStart":false});
            var Q8;
            Q8=makeQuery(id+"F28.opExtrude","CAP_EDGE",EDGE,{"disambiguationData":[OSD([sQuery(id+"F27.wireOp",EDGE,"E71")])],"isStart":false});
            var Q9;
            Q9=makeQuery(id+"F28.opExtrude","CAP_EDGE",EDGE,{"disambiguationData":[OSD([sQuery(id+"F27.wireOp",EDGE,"E68")])],"isStart":false});
            var Q10;
            Q10=makeQuery(id+"F28.opExtrude","CAP_EDGE",EDGE,{"disambiguationData":[OSD([sQuery(id+"F27.wireOp",EDGE,"E67")])],"isStart":false});
            var Q11;
            Q11=makeQuery(id+"F28.opExtrude","CAP_EDGE",EDGE,{"disambiguationData":[OSD([sQuery(id+"F27.wireOp",EDGE,"E64")])],"isStart":false});
            fillet(context, id + "F29", {"entities" : qUnion([Q0, Q1, Q2, Q3, Q4, Q5, Q6, Q7, Q8, Q9, Q10, Q11]), "radius" : 0.25 * mm, "tangentPropagation" : true, "allowEdgeOverflow" : false});
        }
    });
